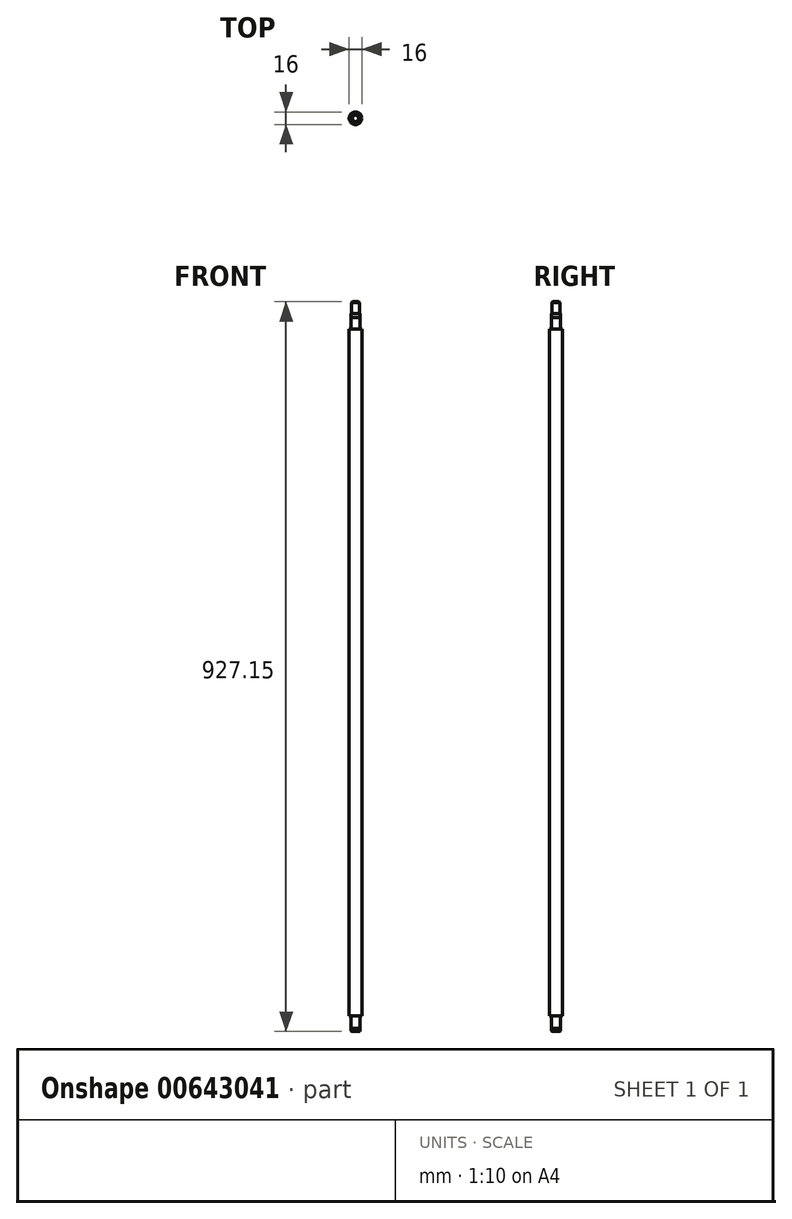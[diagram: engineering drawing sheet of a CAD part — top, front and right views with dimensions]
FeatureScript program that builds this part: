
annotation { "Feature Type Name" : "Feature", "Feature Type Description" : "" }
export const myFeature = defineFeature(function(context is Context, id is Id, definition is map)
    precondition{}
    {
        {
            var Q0;
            Q0=qCreatedBy(makeId("Top.planeOp"),FACE);
            var sketch = newSketch(context, id + "F0", { "sketchPlane" : qUnion([Q0])});
            skCircle(sketch, "E0", {"center": v(0, 0) * mm, "radius": 6 * mm});
            skSolve(sketch);
        }
        {
            var Q0;
            Q0=makeQuery(id+"F0.imprint","IMPRINT",FACE,{"disambiguationData":[TD([[makeQuery(id+"F0.imprint","IMPRINT",EDGE,{"derivedFrom":sQuery(id+"F0.wireOp",EDGE,"E0")}),1.0]])]});
            extrude(context, id + "F1", {"entities" : qUnion([Q0]), "depth" : 3 * mm});
        }
        {
            var Q0;
            Q0=makeQuery(id+"F1.opExtrude","CAP_FACE",FACE,{"disambiguationData":[OSD([sQuery(id+"F0.wireOp",EDGE,"E0")])],"isStart":false});
            var sketch = newSketch(context, id + "F2", { "sketchPlane" : qUnion([Q0])});
            skCircle(sketch, "E1", {"center": v(0, 0) * mm, "radius": 5.75 * mm});
            skSolve(sketch);
        }
        {
            var Q0;
            Q0=makeQuery(id+"F2.imprint","IMPRINT",FACE,{"disambiguationData":[TD([[makeQuery(id+"F2.imprint","IMPRINT",EDGE,{"derivedFrom":sQuery(id+"F2.wireOp",EDGE,"E1")}),1.0]])]});
            extrude(context, id + "F3", {"entities" : qUnion([Q0]), "operationType" : NewBodyOperationType.ADD, "depth" : 1.15 * mm});
        }
        {
            var Q0;
            Q0=makeQuery(id+"F3.opExtrude","CAP_FACE",FACE,{"disambiguationData":[OSD([sQuery(id+"F2.wireOp",EDGE,"E1")])],"isStart":false});
            var sketch = newSketch(context, id + "F4", { "sketchPlane" : qUnion([Q0])});
            skCircle(sketch, "E2", {"center": v(0, 0) * mm, "radius": 6 * mm});
            skSolve(sketch);
        }
        {
            var Q0;
            Q0=makeQuery(id+"F4.imprint","IMPRINT",FACE,{"disambiguationData":[TD([[makeQuery(id+"F4.imprint","IMPRINT",EDGE,{"derivedFrom":sQuery(id+"F4.wireOp",EDGE,"E2")}),1.0]])]});
            var Q1;
            Q1=makeQuery(id+"F4.imprint","IMPRINT",FACE,{"disambiguationData":[TD([[makeQuery(id+"F4.imprint","IMPRINT",EDGE,{"derivedFrom":makeQuery(id+"F3.opExtrude","CAP_EDGE",EDGE,{"disambiguationData":[OSD([sQuery(id+"F2.wireOp",EDGE,"E1")])],"isStart":false})}),1.0]])]});
            extrude(context, id + "F5", {"entities" : qUnion([Q0, Q1]), "operationType" : NewBodyOperationType.ADD, "depth" : 16 * mm});
        }
        {
            var Q0;
            Q0=makeQuery(id+"F5.opExtrude","CAP_FACE",FACE,{"disambiguationData":[OSD([sQuery(id+"F4.wireOp",EDGE,"E2")])],"isStart":false});
            var sketch = newSketch(context, id + "F6", { "sketchPlane" : qUnion([Q0])});
            skCircle(sketch, "E3", {"center": v(0, 0) * mm, "radius": 8 * mm});
            skSolve(sketch);
        }
        {
            var Q0;
            Q0=makeQuery(id+"F6.imprint","IMPRINT",FACE,{"disambiguationData":[TD([[makeQuery(id+"F6.imprint","IMPRINT",EDGE,{"derivedFrom":sQuery(id+"F6.wireOp",EDGE,"E3")}),1.0]])]});
            var Q1;
            Q1=makeQuery(id+"F6.imprint","IMPRINT",FACE,{"disambiguationData":[TD([[makeQuery(id+"F6.imprint","IMPRINT",EDGE,{"derivedFrom":makeQuery(id+"F5.opExtrude","CAP_EDGE",EDGE,{"disambiguationData":[OSD([sQuery(id+"F4.wireOp",EDGE,"E2")])],"isStart":false})}),1.0]])]});
            extrude(context, id + "F7", {"entities" : qUnion([Q0, Q1]), "operationType" : NewBodyOperationType.ADD, "depth" : 872 * mm});
        }
        {
            var Q0;
            Q0=makeQuery(id+"F7.opExtrude","CAP_FACE",FACE,{"disambiguationData":[OSD([sQuery(id+"F6.wireOp",EDGE,"E3")])],"isStart":false});
            var sketch = newSketch(context, id + "F8", { "sketchPlane" : qUnion([Q0])});
            skCircle(sketch, "E4", {"center": v(0, 0) * mm, "radius": 6 * mm});
            skSolve(sketch);
        }
        {
            var Q0;
            Q0=makeQuery(id+"F8.imprint","IMPRINT",FACE,{"disambiguationData":[TD([[makeQuery(id+"F8.imprint","IMPRINT",EDGE,{"derivedFrom":sQuery(id+"F8.wireOp",EDGE,"E4")}),1.0]])]});
            extrude(context, id + "F9", {"entities" : qUnion([Q0]), "operationType" : NewBodyOperationType.ADD, "depth" : 15 * mm, "offsetDistance" : 25 * mm});
        }
        {
            var Q0;
            Q0=makeQuery(id+"F9.opExtrude","CAP_FACE",FACE,{"disambiguationData":[OSD([sQuery(id+"F8.wireOp",EDGE,"E4")])],"isStart":false});
            var sketch = newSketch(context, id + "F10", { "sketchPlane" : qUnion([Q0])});
            skCircle(sketch, "E5", {"center": v(0, 0) * mm, "radius": 5.95 * mm});
            skSolve(sketch);
        }
        {
            var Q0;
            Q0=makeQuery(id+"F10.imprint","IMPRINT",FACE,{"disambiguationData":[TD([[makeQuery(id+"F10.imprint","IMPRINT",EDGE,{"derivedFrom":sQuery(id+"F10.wireOp",EDGE,"E5")}),1.0]])]});
            extrude(context, id + "F11", {"entities" : qUnion([Q0]), "operationType" : NewBodyOperationType.ADD, "depth" : 2 * mm, "offsetDistance" : 25 * mm});
        }
        {
            var Q0;
            Q0=makeQuery(id+"F11.opExtrude","CAP_FACE",FACE,{"disambiguationData":[OSD([sQuery(id+"F10.wireOp",EDGE,"E5")])],"isStart":false});
            var sketch = newSketch(context, id + "F12", { "sketchPlane" : qUnion([Q0])});
            skCircle(sketch, "E6", {"center": v(0, 0) * mm, "radius": 5.95 * mm});
            skSolve(sketch);
        }
        {
            var Q0;
            Q0=makeQuery(id+"F12.imprint","IMPRINT",FACE,{"disambiguationData":[TD([[makeQuery(id+"F12.imprint","IMPRINT",EDGE,{"derivedFrom":sQuery(id+"F12.wireOp",EDGE,"E6")}),1.0]])]});
            extrude(context, id + "F13", {"entities" : qUnion([Q0]), "operationType" : NewBodyOperationType.ADD, "depth" : 3 * mm, "offsetDistance" : 25 * mm});
        }
        {
            var Q0;
            Q0=makeQuery(id+"F13.opExtrude","CAP_FACE",FACE,{"disambiguationData":[OSD([sQuery(id+"F12.wireOp",EDGE,"E6")])],"isStart":false});
            var sketch = newSketch(context, id + "F14", { "sketchPlane" : qUnion([Q0])});
            skCircle(sketch, "E7", {"center": v(0, 0) * mm, "radius": 5 * mm});
            skSolve(sketch);
        }
        {
            var Q0;
            Q0=makeQuery(id+"F14.imprint","IMPRINT",FACE,{"disambiguationData":[TD([[makeQuery(id+"F14.imprint","IMPRINT",EDGE,{"derivedFrom":sQuery(id+"F14.wireOp",EDGE,"E7")}),1.0]])]});
            extrude(context, id + "F15", {"entities" : qUnion([Q0]), "operationType" : NewBodyOperationType.ADD, "depth" : 15 * mm});
        }
        {
            var Q0;
            Q0=makeQuery(id+"F15.opExtrude","CAP_EDGE",EDGE,{"disambiguationData":[OSD([sQuery(id+"F14.wireOp",EDGE,"E7")])],"isStart":false});
            var Q1;
            Q1=makeQuery(id+"F1.opExtrude","CAP_EDGE",EDGE,{"disambiguationData":[OSD([sQuery(id+"F0.wireOp",EDGE,"E0")])],"isStart":true});
            chamfer(context, id + "F16", {"entities" : qUnion([Q0, Q1]), "width" : 1 * mm, "tangentPropagation" : true});
        }
    });
